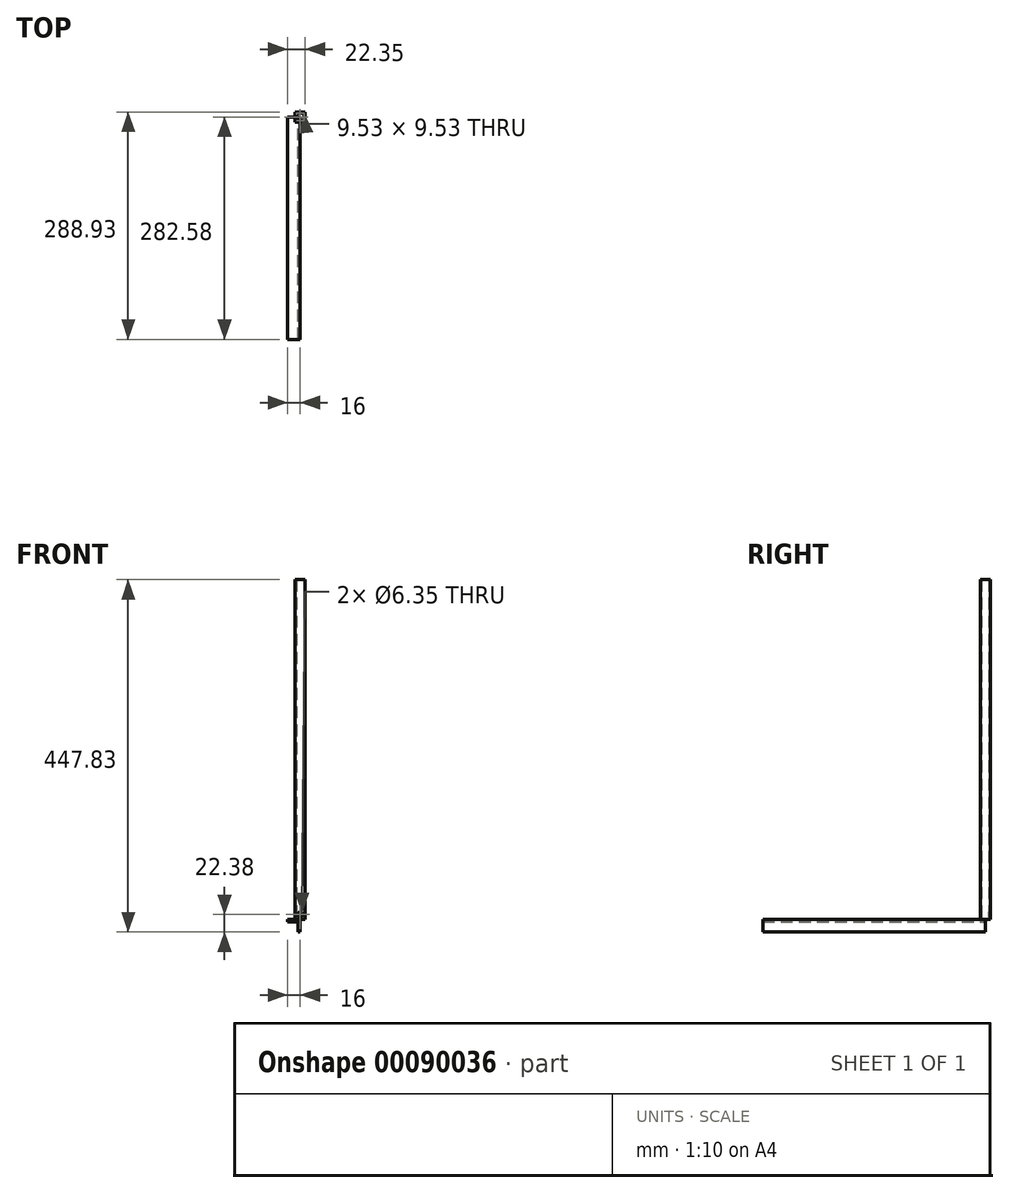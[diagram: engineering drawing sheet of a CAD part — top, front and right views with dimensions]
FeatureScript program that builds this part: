
annotation { "Feature Type Name" : "Feature", "Feature Type Description" : "" }
export const myFeature = defineFeature(function(context is Context, id is Id, definition is map)
    precondition{}
    {
        {
            var Q0;
            Q0=qCreatedBy(makeId("Top.planeOp"),FACE);
            var sketch = newSketch(context, id + "F0", { "sketchPlane" : qUnion([Q0])});
            skLineSegment(sketch, "E0.bottom", {"start": v(6.35, 6.35) * mm, "end": v(-6.35, 6.35) * mm});
            skLineSegment(sketch, "E0.top", {"start": v(6.35, -6.35) * mm, "end": v(-6.35, -6.35) * mm});
            skLineSegment(sketch, "E0.left", {"start": v(6.35, 6.35) * mm, "end": v(6.35, -6.35) * mm});
            skLineSegment(sketch, "E0.right", {"start": v(-6.35, 6.35) * mm, "end": v(-6.35, -6.35) * mm});
            skPoint(sketch, "E0.middle", {"position": v(0, 0) * mm});
            skLineSegment(sketch, "E1.0", {"start": v(-4.76, 4.76) * mm, "end": v(-4.76, -4.76) * mm});
            skLineSegment(sketch, "E1.1", {"start": v(4.76, 4.76) * mm, "end": v(-4.76, 4.76) * mm});
            skLineSegment(sketch, "E1.2", {"start": v(4.76, 4.76) * mm, "end": v(4.76, -4.76) * mm});
            skLineSegment(sketch, "E1.3", {"start": v(4.76, -4.76) * mm, "end": v(-4.76, -4.76) * mm});
            skSolve(sketch);
        }
        {
            var Q0;
            Q0 = qSketchRegion(id + "F0", true);
            extrude(context, id + "F1", {"entities" : qUnion([Q0]), "depth" : 431.8 * mm});
        }
        {
            var Q0;
            Q0=makeQuery(id+"F1.opExtrude","SWEPT_FACE",FACE,{"disambiguationData":[OSD([sQuery(id+"F0.wireOp",EDGE,"E0.bottom")])]});
            var sketch = newSketch(context, id + "F2", { "sketchPlane" : qUnion([Q0])});
            skCircle(sketch, "E2", {"center": v(0, 6.35) * mm, "radius": 3.18 * mm});
            skPoint(sketch, "E2.centerSnap0", {"position": v(0, 0) * mm});
            skSolve(sketch);
        }
        {
            var Q0;
            Q0 = qSketchRegion(id + "F2", true);
            extrude(context, id + "F3", {"entities" : qUnion([Q0]), "operationType" : NewBodyOperationType.REMOVE, "endBound" : BoundingType.THROUGH_ALL, "oppositeDirection" : true, "depth" : 25.4 * mm});
        }
        {
            var Q0;
            Q0=qCreatedBy(makeId("Front.planeOp"),FACE);
            var sketch = newSketch(context, id + "F4", { "sketchPlane" : qUnion([Q0])});
            skLineSegment(sketch, "E3", {"start": v(0, -0.03) * mm, "end": v(0, -16.03) * mm});
            skLineSegment(sketch, "E4", {"start": v(0, -16.03) * mm, "end": v(-3, -16.03) * mm});
            skLineSegment(sketch, "E5", {"start": v(-3, -16.03) * mm, "end": v(-3, -3.03) * mm});
            skLineSegment(sketch, "E6", {"start": v(-3, -3.03) * mm, "end": v(-16, -3.03) * mm});
            skLineSegment(sketch, "E7", {"start": v(-16, -3.03) * mm, "end": v(-16, -0.03) * mm});
            skLineSegment(sketch, "E8", {"start": v(-16, -0.03) * mm, "end": v(0, -0.03) * mm});
            skSolve(sketch);
        }
        {
            var Q0;
            Q0 = qSketchRegion(id + "F4", true);
            extrude(context, id + "F5", {"entities" : qUnion([Q0]), "depth" : 282.57 * mm});
        }
    });
